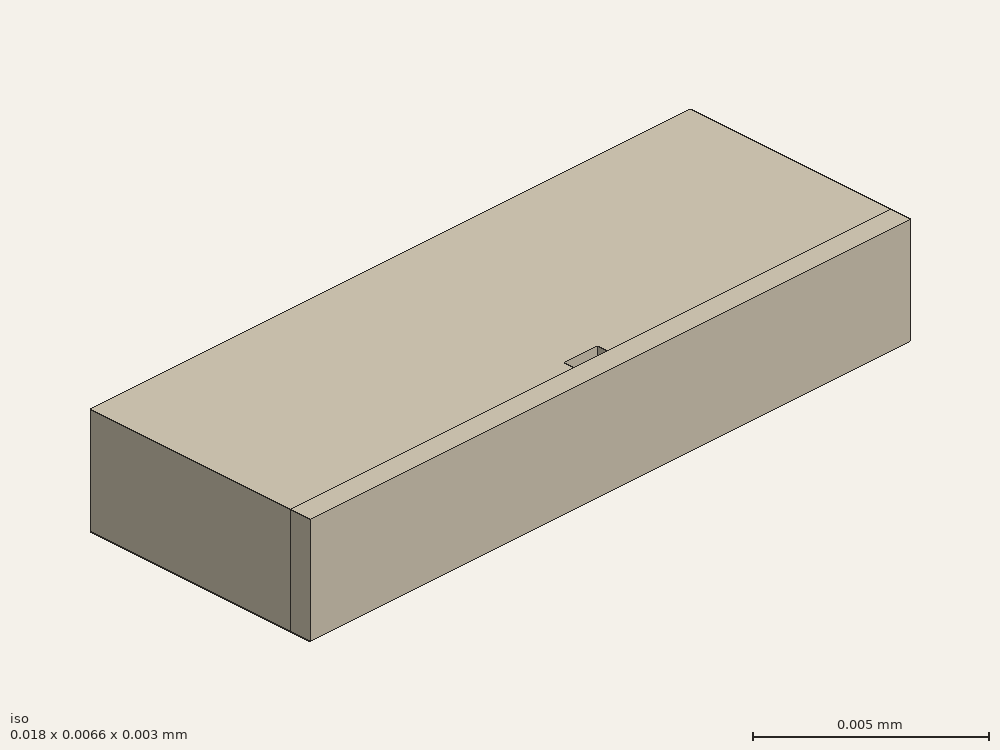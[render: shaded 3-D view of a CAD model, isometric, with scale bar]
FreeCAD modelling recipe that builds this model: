
FCSTD DOCUMENT  (FreeCAD 0.21R33694 (Git))
Label: strip
License: All rights reserved
LicenseURL: http://en.wikipedia.org/wiki/All_rights_reserved
objects: Part::Part2DObjectPython×9, App::FeaturePython×6, Part::Extrusion×3, Part::Cut×1, Part::FeaturePython×1
note: 14 computed .brp shape members not serialized (recipe doc carries the construction recipe); baked Part::Feature solids carry a one-line shape summary decoded from their .brp

FEATURE [Part::Part2DObjectPython] Rectangle  # Draft 2D object (typed FeaturePython)
  Area = 1.143e-05
  ChamferSize = 0
  Columns = 1
  FilletRadius = 0
  Height = 0.000635
  Length = 0.018
  MakeFace = true
  Placement = pos=(-0.009,0,0) rot=(0,0,1;0rad)
  Rows = 1
FEATURE [Part::Part2DObjectPython] Rectangle001  # Draft 2D object (typed FeaturePython)
  Area = 0.000108
  ChamferSize = 0
  Columns = 1
  FilletRadius = 0
  Height = 0.006
  Length = 0.018
  MakeFace = true
  Placement = pos=(-0.009,0.000635,0) rot=(0,0,1;0rad)
  Rows = 1
FEATURE [Part::Part2DObjectPython] Rectangle002  # Draft 2D object (typed FeaturePython)
  Area = 3e-07
  ChamferSize = 0
  Columns = 1
  FilletRadius = 0
  Height = 0.0003
  Length = 0.001
  MakeFace = true
  Placement = pos=(-0.0005,0.000635,0) rot=(0,0,1;0rad)
  Rows = 1
FEATURE [Part::Extrusion] Extrude  label="substrate1"
  Base = -> Rectangle
  Dir = (0,0,1)
  DirMode = 2
  FaceMakerClass = Part::FaceMakerBullseye
  LengthFwd = 0.003
  LengthRev = 0
  Solid = false
  Symmetric = false
FEATURE [Part::Extrusion] Extrude001
  Base = -> Rectangle002
  Dir = (0,0,1)
  DirMode = 2
  FaceMakerClass = Part::FaceMakerBullseye
  LengthFwd = 0.003
  LengthRev = 0
  Solid = false
  Symmetric = false
FEATURE [Part::Extrusion] Extrude002
  Base = -> Rectangle001
  Dir = (0,0,1)
  DirMode = 2
  FaceMakerClass = Part::FaceMakerBullseye
  LengthFwd = 0.003
  LengthRev = 0
  Solid = false
  Symmetric = false
FEATURE [Part::Cut] Cut  label="air1"
  Base = -> Extrude002
  Tool = -> Extrude001
FEATURE [Part::Part2DObjectPython] Rectangle003  label="_Pport1"  # Draft 2D object (typed FeaturePython)
  Area = 0.00011943
  ChamferSize = 0
  Columns = 1
  FilletRadius = 0
  Height = 0.006635
  Length = 0.018
  MakeFace = true
  Placement = pos=(-0.009,0,0.003) rot=(0,0,1;0rad)
  Rows = 1
FEATURE [Part::Part2DObjectPython] Rectangle004  label="_Pi1"  # Draft 2D object (typed FeaturePython)
  Area = 3e-07
  ChamferSize = 0
  Columns = 1
  FilletRadius = 0
  Height = 0.0003
  Length = 0.001
  MakeFace = true
  Placement = pos=(-0.0005,0.000635,0.003) rot=(0,0,1;0rad)
  Rows = 1
FEATURE [Part::Part2DObjectPython] Line  label="_Pv1"  # Draft 2D object (typed FeaturePython)
  Area = 0
  ChamferSize = 0
  Closed = false
  End = (0,0.000635,0.003)
  FilletRadius = 0
  Length = 0.000635
  MakeFace = true
  Placement = pos=(0,0,0.003) rot=(0,0,1;0rad)
  Points = (2) [(0,0,0),(3.88825e-20,0.000635,0)]
  Start = (0,0,0.003)
  Subdivisions = 0
FEATURE [Part::Part2DObjectPython] Rectangle005  label="_Pport2"  # Draft 2D object (typed FeaturePython)
  Area = 0.00011943
  ChamferSize = 0
  Columns = 1
  FilletRadius = 0
  Height = 0.006635
  Length = 0.018
  MakeFace = true
  Placement = pos=(-0.009,0,0) rot=(0,0,1;0rad)
  Rows = 1
FEATURE [Part::Part2DObjectPython] Rectangle006  label="_Pi2"  # Draft 2D object (typed FeaturePython)
  Area = 3e-07
  ChamferSize = 0
  Columns = 1
  FilletRadius = 0
  Height = 0.0003
  Length = 0.001
  MakeFace = true
  Placement = pos=(-0.0005,0.000635,0) rot=(0,0,1;0rad)
  Rows = 1
FEATURE [Part::Part2DObjectPython] Line001  label="_Pv2"  # Draft 2D object (typed FeaturePython)
  Area = 0
  ChamferSize = 0
  Closed = false
  End = (0,0.000635,0)
  FilletRadius = 0
  Length = 0.000635
  MakeFace = true
  Points = (2) [(0,0,0),(1.77361e-18,0.000635,0)]
  Start = (0,0,0)
  Subdivisions = 0
FEATURE [App::FeaturePython] Text  label="_S1(PI){port1}"  # WARN: FeaturePython — macro-defined, semantics opaque (R4)
  Placement = pos=(-0.0005,0.00209073,-0.00864056) rot=(0.57735,0.57735,0.57735;2.0944rad)
  Text = .
FEATURE [App::FeaturePython] Text001  label="_S2(PI){port2}"  # WARN: FeaturePython — macro-defined, semantics opaque (R4)
  Placement = pos=(-0.0005,0.00209073,-0.00864056) rot=(0.57735,0.57735,0.57735;2.0944rad)
  Text = .
FEATURE [App::FeaturePython] Text002  label="_L1(1,voltage){v1}"  # WARN: FeaturePython — macro-defined, semantics opaque (R4)
  Placement = pos=(-0.0005,0.00209073,-0.00864056) rot=(0.57735,0.57735,0.57735;2.0944rad)
  Text = .
FEATURE [App::FeaturePython] Text003  label="_L1(1,current){i1}"  # WARN: FeaturePython — macro-defined, semantics opaque (R4)
  Placement = pos=(-0.0005,0.00209073,-0.00864056) rot=(0.57735,0.57735,0.57735;2.0944rad)
  Text = .
FEATURE [App::FeaturePython] Text004  label="_L2(2,voltage){v2}"  # WARN: FeaturePython — macro-defined, semantics opaque (R4)
  Placement = pos=(-0.0005,0.00209073,-0.00864056) rot=(0.57735,0.57735,0.57735;2.0944rad)
  Text = .
FEATURE [App::FeaturePython] Text005  label="_L2(2,current){i2}"  # WARN: FeaturePython — macro-defined, semantics opaque (R4)
  Placement = pos=(-0.0005,0.00209073,-0.00864056) rot=(0.57735,0.57735,0.57735;2.0944rad)
  Text = .
FEATURE [Part::FeaturePython] BooleanFragments  # WARN: FeaturePython — macro-defined, semantics opaque (R4)
  Mode = 0
  Objects = -> [Extrude,Cut]
  Tolerance = 0
